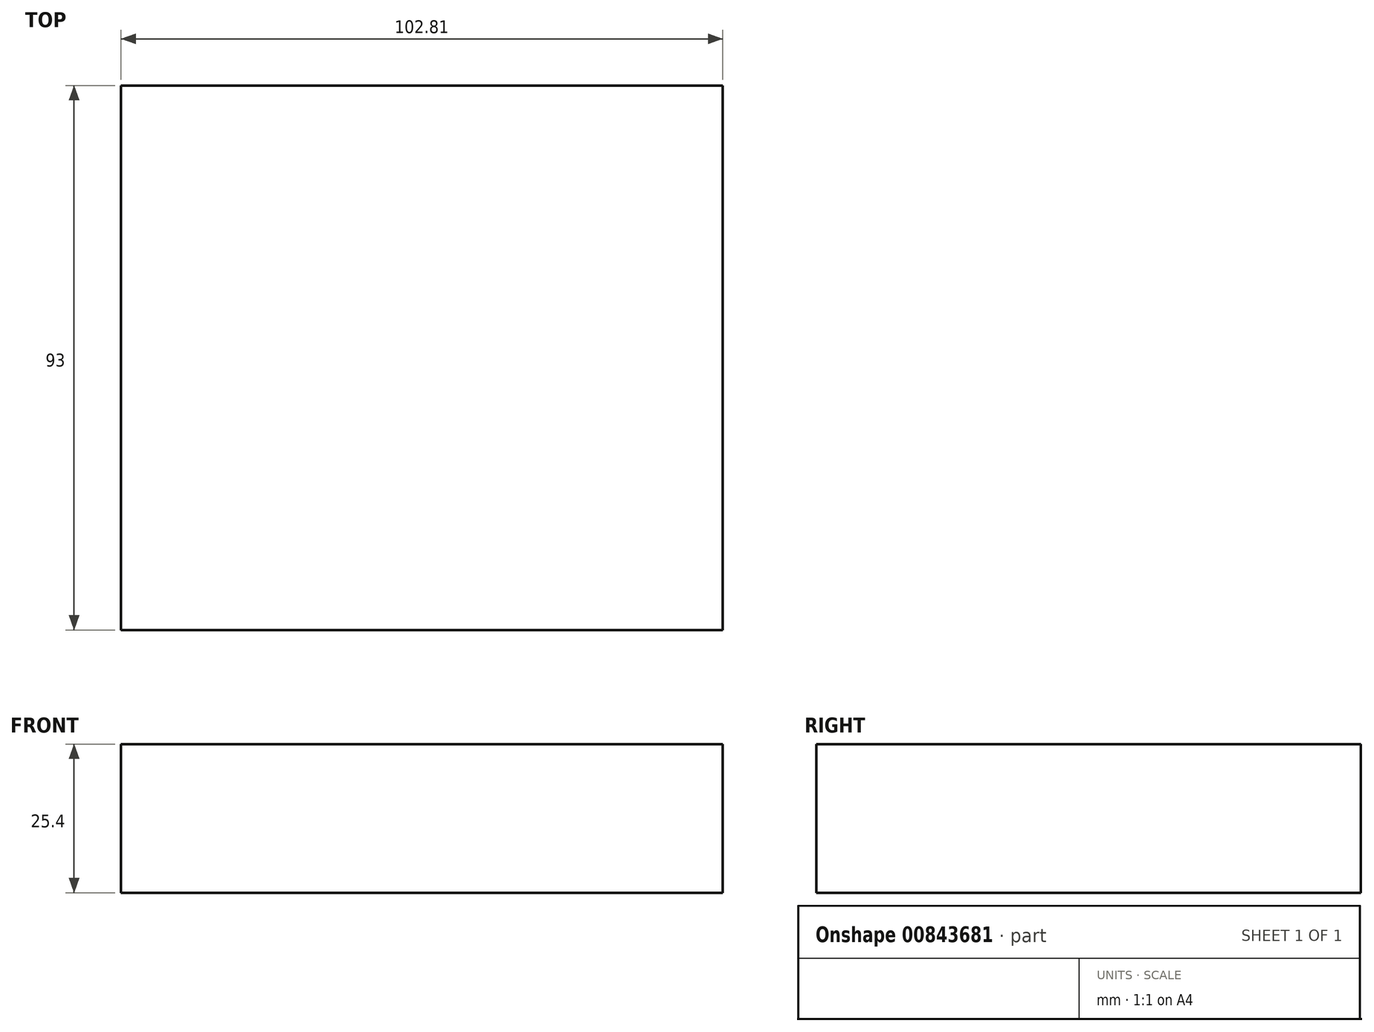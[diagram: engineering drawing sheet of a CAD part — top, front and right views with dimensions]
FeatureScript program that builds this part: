
annotation { "Feature Type Name" : "Feature", "Feature Type Description" : "" }
export const myFeature = defineFeature(function(context is Context, id is Id, definition is map)
    precondition{}
    {
        {
            var Q0;
            Q0=qCreatedBy(makeId("Top.planeOp"),FACE);
            var sketch = newSketch(context, id + "F0", { "sketchPlane" : qUnion([Q0])});
            skLineSegment(sketch, "E0.bottom", {"start": v(43.16, -46.95) * mm, "end": v(-59.65, -46.95) * mm});
            skLineSegment(sketch, "E0.top", {"start": v(43.16, 46.05) * mm, "end": v(-59.65, 46.05) * mm});
            skLineSegment(sketch, "E0.left", {"start": v(43.16, -46.95) * mm, "end": v(43.16, 46.05) * mm});
            skLineSegment(sketch, "E0.right", {"start": v(-59.65, -46.95) * mm, "end": v(-59.65, 46.05) * mm});
            skSolve(sketch);
        }
        {
            var Q0;
            Q0 = qSketchRegion(id + "F0", true);
            extrude(context, id + "F1", {"entities" : qUnion([Q0]), "depth" : 25.4 * mm, "offsetDistance" : 25.4 * mm});
        }
    });
